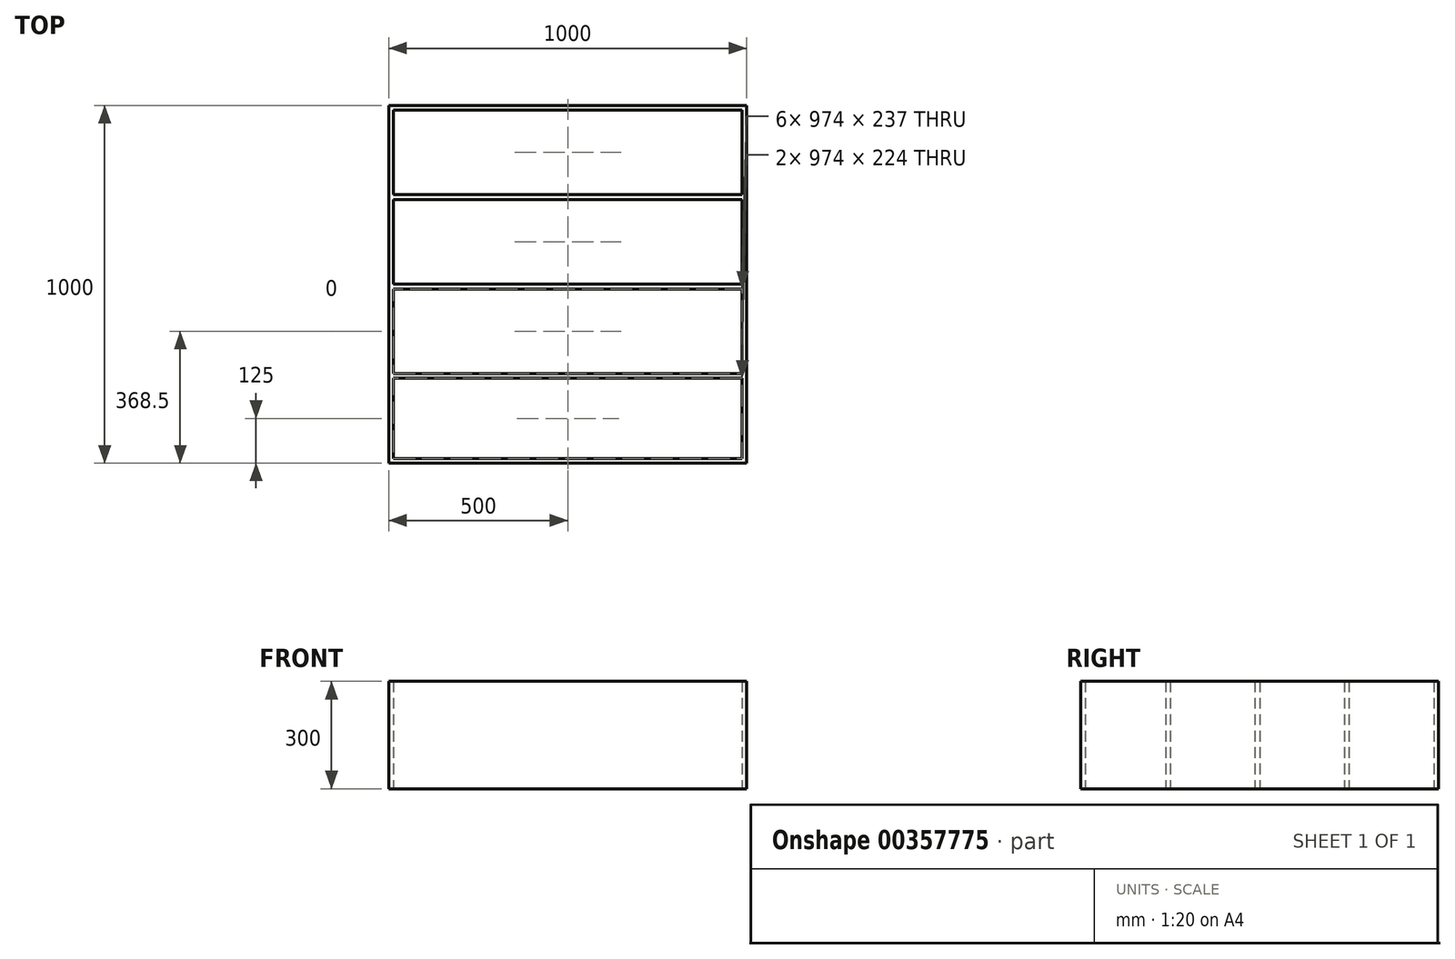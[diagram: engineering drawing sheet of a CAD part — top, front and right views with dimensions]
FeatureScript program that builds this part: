
annotation { "Feature Type Name" : "Feature", "Feature Type Description" : "" }
export const myFeature = defineFeature(function(context is Context, id is Id, definition is map)
    precondition{}
    {
        {
            var Q0;
            Q0=qCreatedBy(makeId("Top.planeOp"),FACE);
            var sketch = newSketch(context, id + "F0", { "sketchPlane" : qUnion([Q0])});
            skLineSegment(sketch, "E0.bottom", {"start": v(0, 0) * mm, "end": v(1000, 0) * mm});
            skLineSegment(sketch, "E0.top", {"start": v(0, 1000) * mm, "end": v(1000, 1000) * mm});
            skLineSegment(sketch, "E0.left", {"start": v(0, 0) * mm, "end": v(0, 1000) * mm});
            skLineSegment(sketch, "E0.right", {"start": v(1000, 0) * mm, "end": v(1000, 1000) * mm});
            skLineSegment(sketch, "E1.0", {"start": v(13, 750) * mm, "end": v(987, 750) * mm});
            skLineSegment(sketch, "E2.0", {"start": v(13, 500) * mm, "end": v(987, 500) * mm});
            skLineSegment(sketch, "E3.0", {"start": v(13, 250) * mm, "end": v(987, 250) * mm});
            skLineSegment(sketch, "E4", {"start": v(0, 750) * mm, "end": v(0, 1000) * mm});
            skLineSegment(sketch, "E5", {"start": v(1000, 750) * mm, "end": v(1000, 1000) * mm});
            skLineSegment(sketch, "E6", {"start": v(1000, 750) * mm, "end": v(1000, 500) * mm});
            skLineSegment(sketch, "E7", {"start": v(1000, 500) * mm, "end": v(1000, 250) * mm});
            skLineSegment(sketch, "E8", {"start": v(0, 250) * mm, "end": v(0, 500) * mm});
            skLineSegment(sketch, "E9", {"start": v(0, 500) * mm, "end": v(0, 750) * mm});
            skLineSegment(sketch, "E10", {"start": v(0, 250) * mm, "end": v(0, 0) * mm});
            skLineSegment(sketch, "E11", {"start": v(1000, 0) * mm, "end": v(1000, 250) * mm});
            skLineSegment(sketch, "E12.0", {"start": v(13, 237) * mm, "end": v(987, 237) * mm});
            skLineSegment(sketch, "E13.0", {"start": v(13, 13) * mm, "end": v(987, 13) * mm});
            skLineSegment(sketch, "E14", {"start": v(0, 13) * mm, "end": v(0, 237) * mm});
            skLineSegment(sketch, "E15", {"start": v(0, 237) * mm, "end": v(0, 13) * mm});
            skLineSegment(sketch, "E16.0", {"start": v(13, 237) * mm, "end": v(13, 13) * mm});
            skLineSegment(sketch, "E17", {"start": v(1000, 13) * mm, "end": v(1000, 237) * mm});
            skLineSegment(sketch, "E18.0", {"start": v(987, 13) * mm, "end": v(987, 237) * mm});
            skLineSegment(sketch, "E19.0", {"start": v(13, 250) * mm, "end": v(13, 500) * mm});
            skLineSegment(sketch, "E20.0", {"start": v(987, 487) * mm, "end": v(987, 250) * mm});
            skLineSegment(sketch, "E21.0", {"start": v(13, 487) * mm, "end": v(987, 487) * mm});
            skLineSegment(sketch, "E22.0", {"start": v(13, 500) * mm, "end": v(13, 737) * mm});
            skLineSegment(sketch, "E23.0", {"start": v(987, 737) * mm, "end": v(987, 500) * mm});
            skLineSegment(sketch, "E24.0", {"start": v(13, 737) * mm, "end": v(987, 737) * mm});
            skLineSegment(sketch, "E25.0", {"start": v(13, 750) * mm, "end": v(13, 987) * mm});
            skLineSegment(sketch, "E26.0", {"start": v(987, 750) * mm, "end": v(987, 987) * mm});
            skLineSegment(sketch, "E27.0", {"start": v(13, 987) * mm, "end": v(987, 987) * mm});
            skSolve(sketch);
        }
        {
            var Q0;
            {var subQ7=sQuery(id+"F0.wireOp",EDGE,"E0.bottom");Q0=makeQuery(id+"F0.imprint","IMPRINT",FACE,{"disambiguationData":[TD([[makeQuery(id+"F0.imprint","IMPRINT",EDGE,{"derivedFrom":subQ7}),1.0]])]});}
            extrude(context, id + "F1", {"entities" : qUnion([Q0]), "depth" : 300 * mm});
        }
    });
